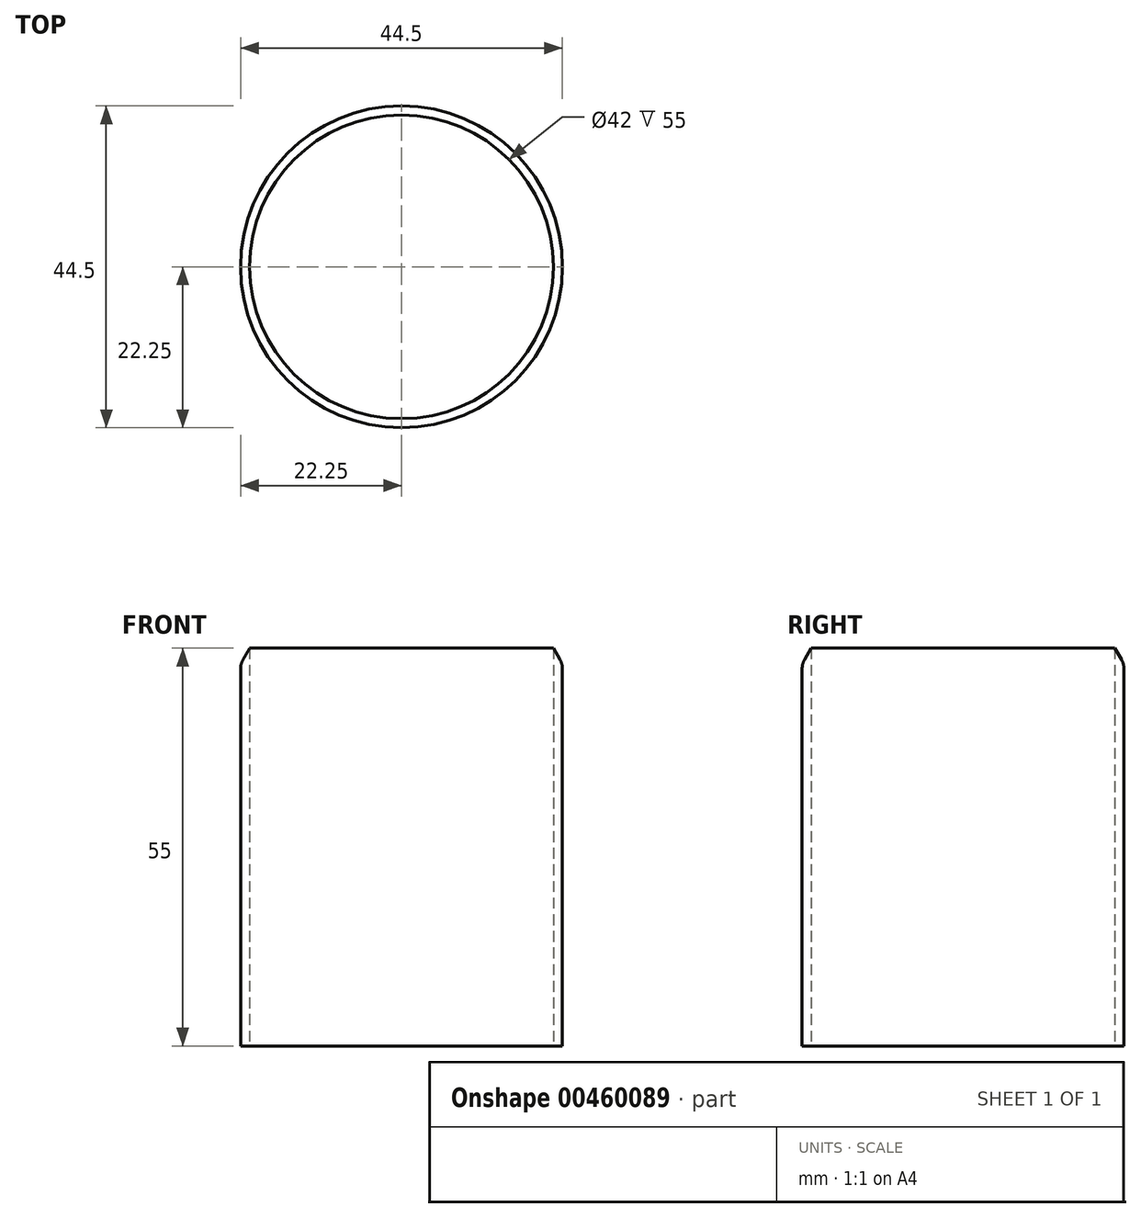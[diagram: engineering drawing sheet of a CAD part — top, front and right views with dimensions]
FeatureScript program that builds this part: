
annotation { "Feature Type Name" : "Feature", "Feature Type Description" : "" }
export const myFeature = defineFeature(function(context is Context, id is Id, definition is map)
    precondition{}
    {
        {
            var Q0;
            Q0=qCreatedBy(makeId("Top.planeOp"),FACE);
            var sketch = newSketch(context, id + "F0", { "sketchPlane" : qUnion([Q0])});
            skCircle(sketch, "E0", {"center": v(0, 0) * mm, "radius": 22.25 * mm});
            skCircle(sketch, "E1.0", {"center": v(0, 0) * mm, "radius": 21 * mm});
            skSolve(sketch);
        }
        {
            var Q0;
            Q0=makeQuery(id+"F0.imprint","IMPRINT",FACE,{"disambiguationData":[TD([[makeQuery(id+"F0.imprint","IMPRINT",EDGE,{"derivedFrom":sQuery(id+"F0.wireOp",EDGE,"E0")}),1.0]])]});
            extrude(context, id + "F1", {"entities" : qUnion([Q0]), "depth" : 55 * mm});
        }
        {
            var Q0;
            Q0=makeQuery(id+"F1.opExtrude","CAP_EDGE",EDGE,{"disambiguationData":[OSD([sQuery(id+"F0.wireOp",EDGE,"E0")])],"isStart":false});
            chamfer(context, id + "F2", {"entities" : qUnion([Q0]), "chamferType" : ChamferType.OFFSET_ANGLE, "width" : 1.25 * mm, "oppositeDirection" : false, "angle" : 60 * degree, "tangentPropagation" : true});
        }
        {
            var Q0;
            {var subQ0=sQuery(id+"F0.wireOp",EDGE,"E0");Q0=makeQuery(id+"F2.opChamfer","BLEND_EDGE",EDGE,{"blendedFrom":[makeQuery(id+"F1.opExtrude","CAP_EDGE",EDGE,{"disambiguationData":[OSD([subQ0])],"isStart":false}),makeQuery(id+"F1.opExtrude","SWEPT_FACE",FACE,{"disambiguationData":[OSD([subQ0])]})],"blendedInto":[makeQuery(id+"F1.opExtrude","SWEPT_FACE",FACE,{"disambiguationData":[OSD([subQ0])]})]});}
            fillet(context, id + "F3", {"entities" : qUnion([Q0]), "radius" : 2.5 * mm, "tangentPropagation" : true, "allowEdgeOverflow" : false});
        }
    });
